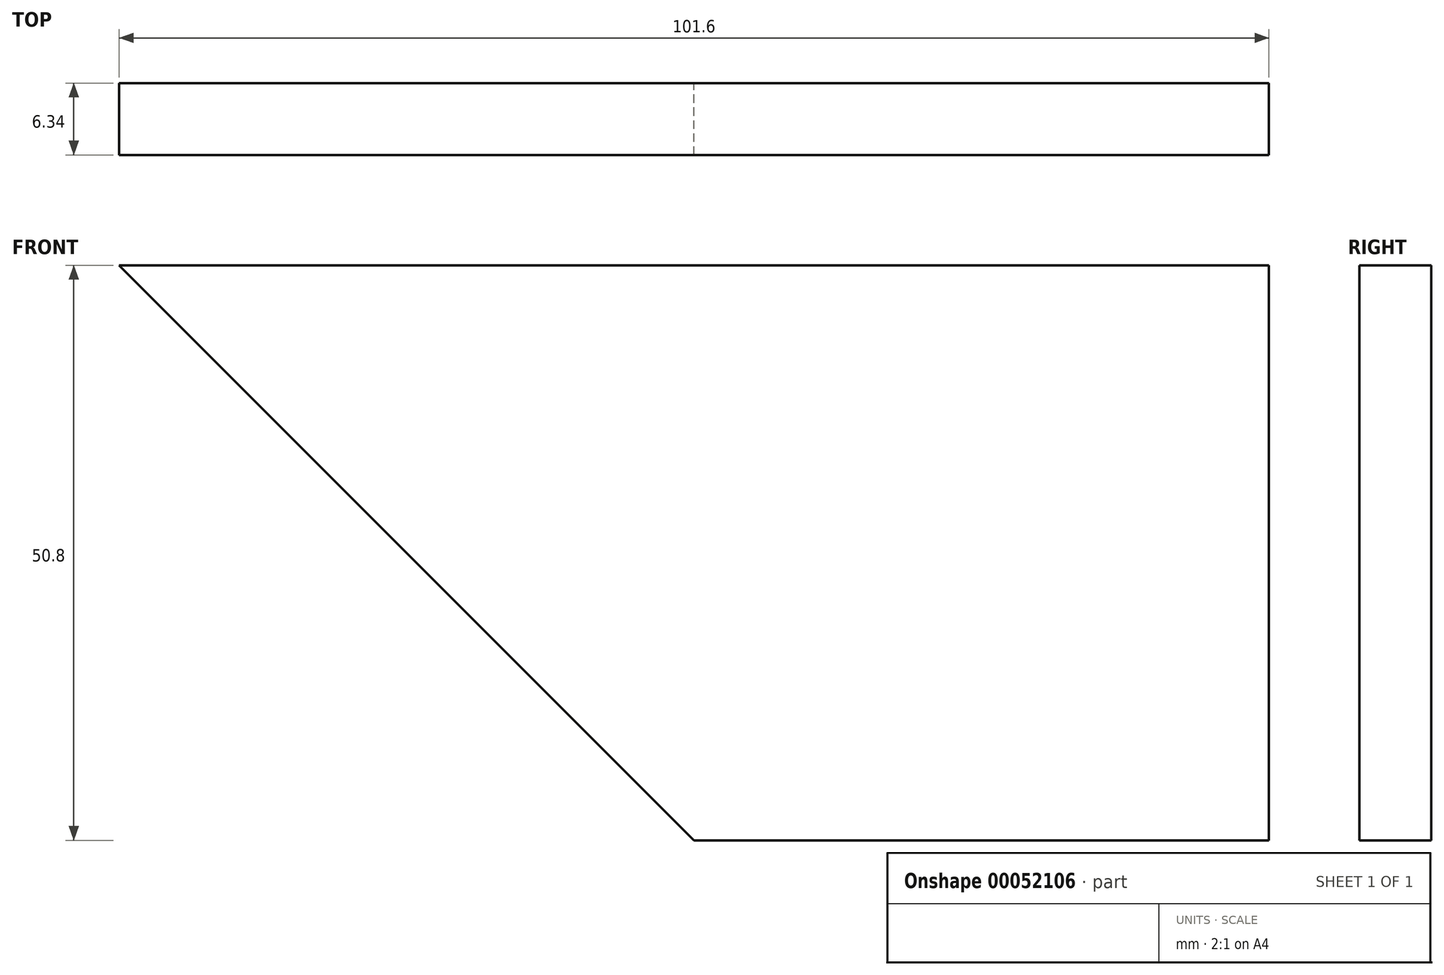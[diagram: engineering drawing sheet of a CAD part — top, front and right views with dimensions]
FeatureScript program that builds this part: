
annotation { "Feature Type Name" : "Feature", "Feature Type Description" : "" }
export const myFeature = defineFeature(function(context is Context, id is Id, definition is map)
    precondition{}
    {
        {
            var Q0;
            Q0=qCreatedBy(makeId("Front.planeOp"),FACE);
            var sketch = newSketch(context, id + "F0", { "sketchPlane" : qUnion([Q0])});
            skLineSegment(sketch, "E0", {"start": v(0, 0) * mm, "end": v(0, 50.8) * mm});
            skLineSegment(sketch, "E1", {"start": v(0, 50.8) * mm, "end": v(-101.6, 50.8) * mm});
            skLineSegment(sketch, "E2", {"start": v(-101.6, 50.8) * mm, "end": v(-50.8, 0) * mm});
            skLineSegment(sketch, "E3", {"start": v(-50.8, 0) * mm, "end": v(0, 0) * mm});
            skSolve(sketch);
        }
        {
            var Q0;
            Q0 = qSketchRegion(id + "F0", true);
            extrude(context, id + "F1", {"entities" : qUnion([Q0]), "endBound" : BoundingType.SYMMETRIC, "depth" : 6.35 * mm});
        }
    });
